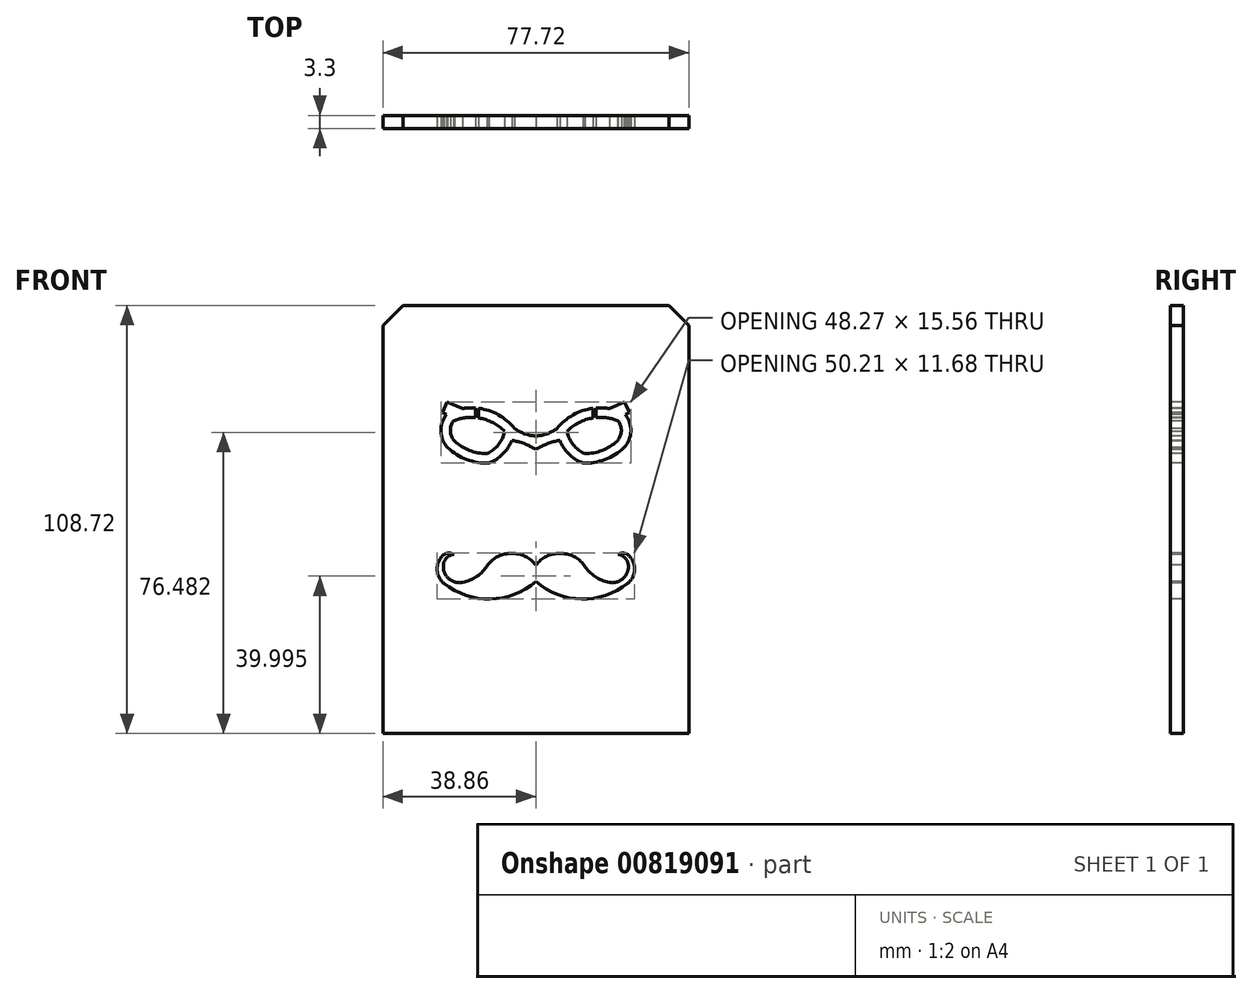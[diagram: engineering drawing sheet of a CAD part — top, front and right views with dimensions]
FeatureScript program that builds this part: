
annotation { "Feature Type Name" : "Feature", "Feature Type Description" : "" }
export const myFeature = defineFeature(function(context is Context, id is Id, definition is map)
    precondition{}
    {
        {
            var Q0;
            Q0=qCreatedBy(makeId("Front.planeOp"),FACE);
            var sketch = newSketch(context, id + "F0", { "sketchPlane" : qUnion([Q0])});
            skLineSegment(sketch, "E0.bottom", {"start": v(38.86, 54.36) * mm, "end": v(-38.86, 54.36) * mm});
            skLineSegment(sketch, "E0.top", {"start": v(38.86, -54.36) * mm, "end": v(-38.86, -54.36) * mm});
            skLineSegment(sketch, "E0.left", {"start": v(38.86, 54.36) * mm, "end": v(38.86, -54.36) * mm});
            skLineSegment(sketch, "E0.right", {"start": v(-38.86, 54.36) * mm, "end": v(-38.86, -54.36) * mm});
            skPoint(sketch, "E0.middle", {"position": v(0, 0) * mm});
            skSolve(sketch);
        }
        {
            var Q0;
            Q0=qSketchRegion(id+"F0",true);
            extrude(context, id + "F1", {"entities" : qUnion([Q0]), "depth" : 3.3 * mm});
        }
        {
            var Q0;
            Q0=makeQuery(id+"F1.opExtrude","CAP_FACE",FACE,{"disambiguationData":[OSD([sQuery(id+"F0.wireOp",EDGE,"E0.bottom"),sQuery(id+"F0.wireOp",EDGE,"E0.top"),sQuery(id+"F0.wireOp",EDGE,"E0.left"),sQuery(id+"F0.wireOp",EDGE,"E0.right")])],"isStart":false});
            var sketch = newSketch(context, id + "F2", { "sketchPlane" : qUnion([Q0])});
            skLineSegment(sketch, "E1", {"start": v(0, 57.24) * mm, "end": v(0, -57.24) * mm, "construction": true});
            skLineSegment(sketch, "E2", {"start": v(-50.8, 0) * mm, "end": v(50.8, 0) * mm, "construction": true});
            skArc(sketch, "E3", {"start": v(35.44, -3.57) * mm, "mid": v(31.46, -11.87) * mm, "end": v(32.26, -21.03) * mm});
            skLineSegment(sketch, "E4", {"start": v(15.88, -44.54) * mm, "end": v(0, -44.54) * mm, "construction": true});
            skArc(sketch, "E5", {"start": v(15.88, -44.54) * mm, "mid": v(30.2, -37.06) * mm, "end": v(32.26, -21.03) * mm});
            skArc(sketch, "E6", {"start": v(15.88, -44.54) * mm, "mid": v(7.78, -45.34) * mm, "end": v(0, -47.71) * mm});
            skArc(sketch, "E7.MirrorCS", {"start": v(-15.87, -44.54) * mm, "mid": v(-7.78, -45.34) * mm, "end": v(0, -47.71) * mm});
            skArc(sketch, "E8.MirrorCS", {"start": v(-15.87, -44.54) * mm, "mid": v(-30.2, -37.06) * mm, "end": v(-32.26, -21.03) * mm});
            skArc(sketch, "E9.MirrorCS", {"start": v(-35.44, -3.57) * mm, "mid": v(-31.46, -11.87) * mm, "end": v(-32.26, -21.03) * mm});
            skArc(sketch, "E10.MirrorCS", {"start": v(-35.44, 3.57) * mm, "mid": v(-31.46, 11.87) * mm, "end": v(-32.26, 21.03) * mm});
            skArc(sketch, "E11.MirrorCS", {"start": v(-15.88, 44.54) * mm, "mid": v(-30.2, 37.06) * mm, "end": v(-32.26, 21.03) * mm});
            skArc(sketch, "E12.MirrorCS", {"start": v(-15.88, 44.54) * mm, "mid": v(-7.78, 45.34) * mm, "end": v(0, 47.71) * mm});
            skArc(sketch, "E13.MirrorCS", {"start": v(15.87, 44.54) * mm, "mid": v(7.78, 45.34) * mm, "end": v(0, 47.71) * mm});
            skArc(sketch, "E14.MirrorCS", {"start": v(15.87, 44.54) * mm, "mid": v(30.2, 37.06) * mm, "end": v(32.26, 21.03) * mm});
            skArc(sketch, "E15.MirrorCS", {"start": v(35.44, 3.57) * mm, "mid": v(31.46, 11.87) * mm, "end": v(32.26, 21.03) * mm});
            skArc(sketch, "E16", {"start": v(35.44, 3.57) * mm, "mid": v(34.41, 0) * mm, "end": v(35.44, -3.57) * mm});
            skPoint(sketch, "E17.orphan", {"position": v(39.69, 0) * mm});
            skArc(sketch, "E18.MirrorCS", {"start": v(-35.44, 3.57) * mm, "mid": v(-34.41, 0) * mm, "end": v(-35.44, -3.57) * mm});
            skPoint(sketch, "E19.orphan", {"position": v(-39.69, 0) * mm});
            skSolve(sketch);
        }
        {
            var Q0;
            Q0=makeQuery(id+"F2.imprint","IMPRINT",FACE,{"disambiguationData":[TD([[makeQuery(id+"F2.imprint","IMPRINT",EDGE,{"derivedFrom":sQuery(id+"F2.wireOp",EDGE,"E3")}),1.0]])]});
            var sketch = newSketch(context, id + "F3", { "sketchPlane" : qUnion([Q0])});
            skFitSpline(sketch, "E20", {"points": [v(-34.74, -25) * mm, v(-17.68, -23.14) * mm, v(0, -25.84) * mm, v(18.3, -28) * mm, v(33.6, -24.4) * mm], "startDerivative": vector(68.08, 28.42) * mm, "endDerivative": vector(41.75, 55.86) * mm});
            skArc(sketch, "E21.0", {"start": v(15.88, -44.54) * mm, "mid": v(28.97, -38.63) * mm, "end": v(33.2, -24.9) * mm});
            skArc(sketch, "E22.0", {"start": v(-15.87, -44.54) * mm, "mid": v(-29.14, -38.43) * mm, "end": v(-33.13, -24.38) * mm});
            skArc(sketch, "E23.0", {"start": v(15.88, -44.54) * mm, "mid": v(7.78, -45.34) * mm, "end": v(0, -47.71) * mm});
            skArc(sketch, "E23.1", {"start": v(-15.87, -44.54) * mm, "mid": v(-7.78, -45.34) * mm, "end": v(0, -47.71) * mm});
            skPoint(sketch, "E24.orphan", {"position": v(-32.26, -21.03) * mm});
            skLineSegment(sketch, "E25.bottom", {"start": v(23.58, -32.65) * mm, "end": v(5.44, -32.65) * mm, "construction": true});
            skLineSegment(sketch, "E25.top", {"start": v(23.58, -12.55) * mm, "end": v(5.44, -12.55) * mm, "construction": true});
            skLineSegment(sketch, "E25.left", {"start": v(23.58, -32.65) * mm, "end": v(23.58, -12.55) * mm, "construction": true});
            skLineSegment(sketch, "E25.right", {"start": v(5.44, -32.65) * mm, "end": v(5.44, -12.55) * mm, "construction": true});
            skArc(sketch, "E26", {"start": v(6.5, -26.77) * mm, "mid": v(6.6, -19.6) * mm, "end": v(5.44, -12.55) * mm});
            skArc(sketch, "E27", {"start": v(23.58, -12.55) * mm, "mid": v(22.47, -20.37) * mm, "end": v(22.78, -28.26) * mm});
            skLineSegment(sketch, "E28", {"start": v(0.57, -13.45) * mm, "end": v(5.44, -12.55) * mm});
            skLineSegment(sketch, "E29", {"start": v(28.46, 0) * mm, "end": v(0.57, 0) * mm, "construction": true});
            skArc(sketch, "E30", {"start": v(-2.4, -8.48) * mm, "mid": v(-2.65, -12) * mm, "end": v(0.57, -13.45) * mm});
            skArc(sketch, "E31", {"start": v(0, -10.42) * mm, "mid": v(-0.23, -8.24) * mm, "end": v(-2.4, -8.48) * mm});
            skArc(sketch, "E32", {"start": v(0, -10.42) * mm, "mid": v(-0.04, -11.92) * mm, "end": v(1.4, -12.35) * mm});
            skArc(sketch, "E33", {"start": v(1.4, -12.35) * mm, "mid": v(5.55, -5.86) * mm, "end": v(0.57, 0) * mm});
            skLineSegment(sketch, "E34", {"start": v(14.51, 0) * mm, "end": v(14.51, -12.55) * mm, "construction": true});
            skArc(sketch, "E35.MirrorCS", {"start": v(27.61, -12.35) * mm, "mid": v(23.47, -5.86) * mm, "end": v(28.46, 0) * mm});
            skLineSegment(sketch, "E36.MirrorCS", {"start": v(28.46, -13.45) * mm, "end": v(23.58, -12.55) * mm});
            skArc(sketch, "E37.MirrorCS", {"start": v(31.42, -8.48) * mm, "mid": v(31.67, -12) * mm, "end": v(28.46, -13.45) * mm});
            skArc(sketch, "E38.MirrorCS", {"start": v(29.02, -10.42) * mm, "mid": v(29.25, -8.24) * mm, "end": v(31.42, -8.48) * mm});
            skArc(sketch, "E39.MirrorCS", {"start": v(29.02, -10.42) * mm, "mid": v(29.06, -11.92) * mm, "end": v(27.61, -12.35) * mm});
            skArc(sketch, "E40", {"start": v(0.57, 0) * mm, "mid": v(5.65, -0.6) * mm, "end": v(10.76, -0.93) * mm});
            skLineSegment(sketch, "E41", {"start": v(10.76, -0.93) * mm, "end": v(8.47, 9.06) * mm});
            skLineSegment(sketch, "E42", {"start": v(8.47, 9.06) * mm, "end": v(6.8, 8.68) * mm});
            skArc(sketch, "E43", {"start": v(7.7, 9.94) * mm, "mid": v(5.6, 10.49) * mm, "end": v(6.8, 8.68) * mm});
            skLineSegment(sketch, "E44", {"start": v(14.51, 0) * mm, "end": v(14.77, 8.31) * mm, "construction": true});
            skLineSegment(sketch, "E45.MirrorCS", {"start": v(18.26, -0.93) * mm, "end": v(21.1, 8.66) * mm});
            skLineSegment(sketch, "E46.MirrorCS", {"start": v(21.1, 8.66) * mm, "end": v(22.75, 8.18) * mm});
            skArc(sketch, "E47.MirrorCS", {"start": v(21.93, 9.5) * mm, "mid": v(24.07, 9.9) * mm, "end": v(22.75, 8.18) * mm});
            skArc(sketch, "E48", {"start": v(7.7, 9.94) * mm, "mid": v(12.62, 15.22) * mm, "end": v(14.1, 22.28) * mm});
            skArc(sketch, "E49", {"start": v(15.59, 22.28) * mm, "mid": v(17.1, 15.06) * mm, "end": v(21.93, 9.5) * mm});
            skLineSegment(sketch, "E50", {"start": v(14.1, 22.28) * mm, "end": v(12.75, 29.94) * mm});
            skLineSegment(sketch, "E51", {"start": v(12.75, 29.94) * mm, "end": v(10.25, 29.5) * mm});
            skLineSegment(sketch, "E52", {"start": v(10.25, 29.5) * mm, "end": v(10.04, 30.72) * mm});
            skLineSegment(sketch, "E53", {"start": v(10.04, 30.72) * mm, "end": v(12.66, 31.3) * mm});
            skLineSegment(sketch, "E54", {"start": v(12.66, 31.3) * mm, "end": v(12.12, 34.79) * mm});
            skLineSegment(sketch, "E55", {"start": v(12.12, 34.79) * mm, "end": v(14.24, 35.11) * mm});
            skLineSegment(sketch, "E56", {"start": v(14.24, 35.11) * mm, "end": v(14.8, 31.45) * mm});
            skLineSegment(sketch, "E57", {"start": v(14.8, 31.45) * mm, "end": v(17.72, 31.9) * mm});
            skLineSegment(sketch, "E58", {"start": v(17.72, 31.9) * mm, "end": v(17.99, 30.17) * mm});
            skLineSegment(sketch, "E59", {"start": v(17.99, 30.17) * mm, "end": v(14.89, 29.68) * mm});
            skLineSegment(sketch, "E60", {"start": v(14.89, 29.68) * mm, "end": v(15.59, 22.28) * mm});
            skArc(sketch, "E61.trimOffspring", {"start": v(18.26, -0.93) * mm, "mid": v(23.37, -0.6) * mm, "end": v(28.46, 0) * mm});
            skPoint(sketch, "E62.orphan", {"position": v(18.2, -1.17) * mm});
            skLineSegment(sketch, "E63", {"start": v(8.48, -4.98) * mm, "end": v(9.12, -7.41) * mm});
            skLineSegment(sketch, "E64", {"start": v(9.77, -9.85) * mm, "end": v(10.94, -9.54) * mm});
            skLineSegment(sketch, "E65", {"start": v(12.72, -9.06) * mm, "end": v(12.26, -7.34) * mm});
            skLineSegment(sketch, "E66", {"start": v(11.56, -4.7) * mm, "end": v(10.33, -4.82) * mm});
            skLineSegment(sketch, "E67", {"start": v(9.75, -4.87) * mm, "end": v(10.34, -7.13) * mm});
            skLineSegment(sketch, "E68", {"start": v(10.34, -7.13) * mm, "end": v(9.12, -7.41) * mm});
            skLineSegment(sketch, "E69", {"start": v(10.33, -4.82) * mm, "end": v(10.9, -7.06) * mm});
            skLineSegment(sketch, "E70", {"start": v(10.9, -7.06) * mm, "end": v(12.14, -6.89) * mm});
            skLineSegment(sketch, "E71", {"start": v(9.29, -8.05) * mm, "end": v(10.46, -7.73) * mm});
            skLineSegment(sketch, "E72", {"start": v(10.46, -7.73) * mm, "end": v(10.94, -9.54) * mm});
            skLineSegment(sketch, "E73", {"start": v(11.57, -9.37) * mm, "end": v(11.12, -7.64) * mm});
            skLineSegment(sketch, "E74", {"start": v(11.12, -7.64) * mm, "end": v(12.26, -7.34) * mm});
            skLineSegment(sketch, "E75.trimOffspring", {"start": v(12.14, -6.89) * mm, "end": v(11.56, -4.7) * mm});
            skLineSegment(sketch, "E76.trimOffspring", {"start": v(9.75, -4.87) * mm, "end": v(8.48, -4.98) * mm});
            skLineSegment(sketch, "E77.trimOffspring", {"start": v(9.29, -8.05) * mm, "end": v(9.77, -9.85) * mm});
            skLineSegment(sketch, "E78.trimOffspring", {"start": v(11.57, -9.37) * mm, "end": v(12.72, -9.06) * mm});
            skLineSegment(sketch, "E79.MirrorCS", {"start": v(17.46, -4.7) * mm, "end": v(18.69, -4.82) * mm});
            skLineSegment(sketch, "E80.MirrorCS", {"start": v(19.27, -4.87) * mm, "end": v(18.68, -7.13) * mm});
            skLineSegment(sketch, "E81.MirrorCS", {"start": v(17.45, -9.37) * mm, "end": v(17.9, -7.64) * mm});
            skLineSegment(sketch, "E82.MirrorCS", {"start": v(18.68, -7.13) * mm, "end": v(19.9, -7.41) * mm});
            skLineSegment(sketch, "E83.MirrorCS", {"start": v(17.9, -7.64) * mm, "end": v(16.76, -7.34) * mm});
            skLineSegment(sketch, "E84.MirrorCS", {"start": v(18.69, -4.82) * mm, "end": v(18.12, -7.06) * mm});
            skLineSegment(sketch, "E85.MirrorCS", {"start": v(16.88, -6.89) * mm, "end": v(17.46, -4.7) * mm});
            skLineSegment(sketch, "E86.MirrorCS", {"start": v(18.12, -7.06) * mm, "end": v(16.88, -6.89) * mm});
            skLineSegment(sketch, "E87.MirrorCS", {"start": v(19.27, -4.87) * mm, "end": v(20.54, -4.98) * mm});
            skLineSegment(sketch, "E88.MirrorCS", {"start": v(20.54, -4.98) * mm, "end": v(19.9, -7.41) * mm});
            skLineSegment(sketch, "E89.MirrorCS", {"start": v(19.73, -8.05) * mm, "end": v(18.56, -7.73) * mm});
            skLineSegment(sketch, "E90.MirrorCS", {"start": v(19.73, -8.05) * mm, "end": v(19.25, -9.85) * mm});
            skLineSegment(sketch, "E91.MirrorCS", {"start": v(19.25, -9.85) * mm, "end": v(18.08, -9.54) * mm});
            skLineSegment(sketch, "E92.MirrorCS", {"start": v(18.56, -7.73) * mm, "end": v(18.08, -9.54) * mm});
            skLineSegment(sketch, "E93.MirrorCS", {"start": v(17.45, -9.37) * mm, "end": v(16.3, -9.06) * mm});
            skLineSegment(sketch, "E94.MirrorCS", {"start": v(16.3, -9.06) * mm, "end": v(16.76, -7.34) * mm});
            skArc(sketch, "E95", {"start": v(14.28, 11.97) * mm, "mid": v(12.23, 10.98) * mm, "end": v(11.15, 8.98) * mm});
            skLineSegment(sketch, "E96", {"start": v(14.28, 11.97) * mm, "end": v(14.28, 8.98) * mm});
            skLineSegment(sketch, "E97", {"start": v(15.17, 4.65) * mm, "end": v(15.17, 7.88) * mm});
            skLineSegment(sketch, "E98", {"start": v(18.4, 8.98) * mm, "end": v(15.17, 8.98) * mm});
            skLineSegment(sketch, "E99", {"start": v(11.1, 7.88) * mm, "end": v(14.28, 7.88) * mm});
            skLineSegment(sketch, "E100.trimOffspring", {"start": v(15.17, 8.98) * mm, "end": v(15.17, 11.98) * mm});
            skLineSegment(sketch, "E101.trimOffspring", {"start": v(15.17, 7.88) * mm, "end": v(18.43, 7.88) * mm});
            skLineSegment(sketch, "E102.trimOffspring", {"start": v(14.28, 7.88) * mm, "end": v(14.28, 4.66) * mm});
            skLineSegment(sketch, "E103.trimOffspring", {"start": v(14.28, 8.98) * mm, "end": v(11.15, 8.98) * mm});
            skArc(sketch, "E104.trimOffspring", {"start": v(11.1, 7.88) * mm, "mid": v(12.14, 5.73) * mm, "end": v(14.28, 4.66) * mm});
            skArc(sketch, "E105.trimOffspring", {"start": v(18.4, 8.98) * mm, "mid": v(17.28, 11.01) * mm, "end": v(15.17, 11.98) * mm});
            skArc(sketch, "E106.trimOffspring", {"start": v(15.17, 4.65) * mm, "mid": v(17.37, 5.7) * mm, "end": v(18.43, 7.88) * mm});
            skLineSegment(sketch, "E107.left", {"start": v(12.04, -27.4) * mm, "end": v(12.04, -21.48) * mm});
            skLineSegment(sketch, "E107.right", {"start": v(16, -27.8) * mm, "end": v(16, -21.48) * mm});
            skArc(sketch, "E108", {"start": v(16, -21.48) * mm, "mid": v(14.02, -19.5) * mm, "end": v(12.04, -21.48) * mm});
            skLineSegment(sketch, "E109", {"start": v(12.04, -27.4) * mm, "end": v(16, -27.8) * mm});
            skArc(sketch, "E110.0", {"start": v(-35.44, -3.57) * mm, "mid": v(-31.46, -11.87) * mm, "end": v(-32.26, -21.03) * mm, "construction": true});
            skArc(sketch, "E110.1", {"start": v(15.87, 44.54) * mm, "mid": v(7.78, 45.34) * mm, "end": v(0, 47.71) * mm});
            skArc(sketch, "E110.2", {"start": v(-15.88, 44.54) * mm, "mid": v(-30.2, 37.06) * mm, "end": v(-32.26, 21.03) * mm, "construction": true});
            skArc(sketch, "E110.3", {"start": v(-35.44, 3.57) * mm, "mid": v(-34.41, 0) * mm, "end": v(-35.44, -3.57) * mm, "construction": true});
            skArc(sketch, "E110.4", {"start": v(-35.44, 3.57) * mm, "mid": v(-31.46, 11.87) * mm, "end": v(-32.26, 21.03) * mm});
            skArc(sketch, "E110.5", {"start": v(-15.88, 44.54) * mm, "mid": v(-7.78, 45.34) * mm, "end": v(0, 47.71) * mm});
            skArc(sketch, "E111", {"start": v(-17.1, 9.66) * mm, "mid": v(-3.37, 14.89) * mm, "end": v(1.5, 28.74) * mm});
            skArc(sketch, "E112", {"start": v(-17.1, 9.66) * mm, "mid": v(-26.87, 8.42) * mm, "end": v(-35.44, 3.57) * mm});
            skArc(sketch, "E113", {"start": v(15.87, 44.54) * mm, "mid": v(5.2, 39.82) * mm, "end": v(1.5, 28.74) * mm});
            skArc(sketch, "E114.trimOffspring", {"start": v(-15.88, 44.54) * mm, "mid": v(-30.2, 37.06) * mm, "end": v(-32.26, 21.03) * mm});
            skArc(sketch, "E115", {"start": v(-24.92, -22.89) * mm, "mid": v(-23.55, -16.2) * mm, "end": v(-24.4, -9.44) * mm});
            skFitSpline(sketch, "E116", {"points": [v(-24.4, -9.44) * mm, v(-26.98, -10.38) * mm, v(-27.97, -8.39) * mm, v(-29.93, -8.52) * mm, v(-30.92, -6) * mm, v(-32.1, -5.52) * mm, v(-32.53, -4.18) * mm, v(-32.18, -3.27) * mm, v(-31.84, -4.44) * mm, v(-31.05, -4.83) * mm, v(-31.49, -2) * mm, v(-30.88, -2.14) * mm, v(-30.1, -5.05) * mm, v(-29.45, -3.57) * mm, v(-28.71, -3.66) * mm, v(-29.54, -5.78) * mm, v(-29.23, -7.17) * mm, v(-27.54, -7.04) * mm, v(-26.28, -8.52) * mm, v(-24.4, -7.6) * mm], "startDerivative": vector(-46.53, -30.94) * mm, "endDerivative": vector(36.03, 29.74) * mm});
            skArc(sketch, "E117", {"start": v(-24.4, -7.6) * mm, "mid": v(-24.93, -4.98) * mm, "end": v(-25.9, -2.49) * mm});
            skFitSpline(sketch, "E118", {"points": [v(-25.9, -2.49) * mm, v(-27.5, -1.49) * mm, v(-28.76, -1.49) * mm, v(-29.23, 0) * mm, v(-31.14, 0) * mm, v(-30.8, 3.42) * mm, v(-29.97, 3.55) * mm, v(-30.27, 1.77) * mm, v(-29.54, 1.72) * mm, v(-28.8, 4.59) * mm, v(-27.67, 4.37) * mm, v(-28.28, 1.98) * mm, v(-27.84, 0) * mm, v(-27.2, 2.46) * mm, v(-25.9, 2.37) * mm, v(-25.9, 0) * mm, v(-24.11, -2.49) * mm, v(-22.72, -5.26) * mm, v(-21.68, -4.18) * mm, v(-23.16, 1.33) * mm, v(-20.82, 1.46) * mm, v(-20.82, 3.02) * mm], "startDerivative": vector(-33.14, 31.82) * mm, "endDerivative": vector(-15.18, 49.9) * mm});
            skFitSpline(sketch, "E119", {"points": [v(-20.82, 3.02) * mm, v(-19.2, 3.92) * mm, v(-20.04, 5.84) * mm, v(-20.82, 8.3) * mm, v(-20.04, 8.38) * mm, v(-19.62, 6.46) * mm, v(-18.62, 5.34) * mm, v(-18.96, 7.3) * mm, v(-18.2, 7.55) * mm, v(-18.12, 4.13) * mm, v(-19.33, 2.25) * mm, v(-19.46, 0.87) * mm, v(-20.82, 0) * mm, v(-20.04, -3.35) * mm, v(-16.32, 0) * mm, v(-17.1, 1.46) * mm, v(-15.74, 3.02) * mm, v(-15.45, 5.84) * mm, v(-14.49, 5.55) * mm, v(-14.82, 3.02) * mm, v(-14.53, 1.46) * mm, v(-13.36, 4) * mm, v(-12.02, 3.02) * mm, v(-14.2, 0) * mm, v(-17.1, -4.06) * mm, v(-17.1, -7.4) * mm, v(-14.36, -5.44) * mm, v(-14.57, -4.1) * mm, v(-12.78, -3.22) * mm, v(-12.53, -1.68) * mm, v(-10.44, -0.8) * mm, v(-10.27, 1.46) * mm, v(-9.35, 0) * mm, v(-8.6, 3.02) * mm, v(-8.1, 0) * mm, v(-9.44, -1.26) * mm, v(-11.31, -3.26) * mm, v(-13.15, -4.6) * mm, v(-13.36, -6.6) * mm, v(-15.78, -8.94) * mm], "startDerivative": vector(94.65, 30.69) * mm, "endDerivative": vector(-102.82, -69.25) * mm});
            skArc(sketch, "E120", {"start": v(-15.78, -8.94) * mm, "mid": v(-16.8, -16.14) * mm, "end": v(-15.78, -23.34) * mm});
            skFitSpline(sketch, "E121", {"points": [v(-22.4, -11.55) * mm, v(-21.43, -13.07) * mm, v(-21.4, -14.11) * mm, v(-20.72, -14.36) * mm, v(-20.54, -13.59) * mm, v(-20.94, -12.02) * mm, v(-21.71, -11.06) * mm, v(-22.67, -10.07) * mm, v(-22.4, -11.55) * mm]});
            skFitSpline(sketch, "E122", {"points": [v(-18.38, -10.1) * mm, v(-19.09, -11.5) * mm, v(-19.21, -12.7) * mm, v(-19.15, -14.02) * mm, v(-18.84, -14.6) * mm, v(-18.38, -14.05) * mm, v(-18.26, -13.1) * mm, v(-18.56, -12.32) * mm, v(-18.29, -11.28) * mm, v(-17.6, -10.38) * mm, v(-18.38, -10.1) * mm]});
            skFitSpline(sketch, "E123", {"points": [v(-20.3, -15.78) * mm, v(-20.35, -17.1) * mm, v(-20.9, -18.47) * mm, v(-21.8, -19.67) * mm, v(-21.9, -21.46) * mm, v(-20.45, -21.43) * mm, v(-19.64, -20.38) * mm, v(-19.43, -18.84) * mm, v(-19.7, -17.85) * mm, v(-19.7, -16.37) * mm, v(-19.43, -15.38) * mm, v(-20.3, -15.78) * mm]});
            skCircle(sketch, "E124", {"center": v(-15.88, 27.08) * mm, "radius": 13.34 * mm});
            skSolve(sketch);
        }
        {
            var Q0;
            Q0=qSketchRegion(id+"F3",true);
            extrude(context, id + "F4", {"entities" : qUnion([Q0]), "operationType" : NewBodyOperationType.ADD, "oppositeDirection" : true, "depth" : 3.3 * mm});
        }
        {
            var Q0;
            Q0=makeQuery(id+"F1.opExtrude","SWEPT_EDGE",EDGE,{"disambiguationData":[OSD([sQuery(id+"F0.wireOp",EDGE,"E0.bottom"),sQuery(id+"F0.wireOp",EDGE,"E0.right")])]});
            var Q1;
            Q1=makeQuery(id+"F1.opExtrude","SWEPT_EDGE",EDGE,{"disambiguationData":[OSD([sQuery(id+"F0.wireOp",EDGE,"E0.bottom"),sQuery(id+"F0.wireOp",EDGE,"E0.left")])]});
            chamfer(context, id + "F5", {"entities" : qUnion([Q0, Q1]), "width" : 5.08 * mm, "tangentPropagation" : true});
        }
        {
            var Q0;
            Q0=makeQuery(id+"F2.imprint","IMPRINT",FACE,{"disambiguationData":[TD([[makeQuery(id+"F2.imprint","IMPRINT",EDGE,{"derivedFrom":sQuery(id+"F2.wireOp",EDGE,"E3")}),-1.0]])]});
            var sketch = newSketch(context, id + "F6", { "sketchPlane" : qUnion([Q0])});
            skArc(sketch, "E125", {"start": v(6.08, 20.1) * mm, "mid": v(8.4, 16.62) * mm, "end": v(11.92, 14.34) * mm});
            skArc(sketch, "E126", {"start": v(11.92, 14.34) * mm, "mid": v(17.55, 15.25) * mm, "end": v(22.4, 18.27) * mm});
            skArc(sketch, "E127", {"start": v(22.4, 18.27) * mm, "mid": v(24.13, 22.42) * mm, "end": v(22.71, 26.69) * mm});
            skArc(sketch, "E128", {"start": v(18.65, 28.2) * mm, "mid": v(16.98, 28.36) * mm, "end": v(15.3, 28.33) * mm});
            skArc(sketch, "E129.0", {"start": v(20.92, 25.07) * mm, "mid": v(18.16, 25.83) * mm, "end": v(15.3, 25.9) * mm});
            skArc(sketch, "E129.1", {"start": v(20.68, 19.97) * mm, "mid": v(21.72, 22.48) * mm, "end": v(20.92, 25.07) * mm});
            skArc(sketch, "E129.2", {"start": v(12.43, 16.74) * mm, "mid": v(16.86, 17.57) * mm, "end": v(20.68, 19.97) * mm});
            skArc(sketch, "E129.3", {"start": v(7.92, 22.36) * mm, "mid": v(9.5, 19) * mm, "end": v(12.43, 16.74) * mm});
            skArc(sketch, "E130", {"start": v(0, 21.24) * mm, "mid": v(2.83, 21.78) * mm, "end": v(5.38, 23.13) * mm});
            skArc(sketch, "E131", {"start": v(6.08, 20.1) * mm, "mid": v(2.93, 19.26) * mm, "end": v(0, 17.8) * mm});
            skLineSegment(sketch, "E132", {"start": v(18.65, 28.2) * mm, "end": v(22.54, 29.9) * mm});
            skLineSegment(sketch, "E133", {"start": v(22.54, 29.9) * mm, "end": v(23.75, 27.14) * mm});
            skLineSegment(sketch, "E134", {"start": v(23.75, 27.14) * mm, "end": v(22.71, 26.69) * mm});
            skPoint(sketch, "E135.orphan", {"position": v(22.4, 27.06) * mm});
            skArc(sketch, "E136", {"start": v(0, -15.75) * mm, "mid": v(11.58, -20.2) * mm, "end": v(23.33, -16.24) * mm});
            skArc(sketch, "E137", {"start": v(23.33, -16.24) * mm, "mid": v(25.1, -12.56) * mm, "end": v(23.33, -8.89) * mm});
            skArc(sketch, "E138", {"start": v(23.33, -8.89) * mm, "mid": v(22.07, -8.52) * mm, "end": v(20.8, -8.89) * mm});
            skArc(sketch, "E139", {"start": v(23.33, -10.83) * mm, "mid": v(22.38, -9.45) * mm, "end": v(20.8, -8.89) * mm});
            skArc(sketch, "E140", {"start": v(18.65, -15.99) * mm, "mid": v(22.45, -14.73) * mm, "end": v(23.33, -10.83) * mm});
            skArc(sketch, "E141", {"start": v(12.27, -11.6) * mm, "mid": v(15, -14.45) * mm, "end": v(18.65, -15.99) * mm});
            skArc(sketch, "E142", {"start": v(12.27, -11.6) * mm, "mid": v(6.14, -8.58) * mm, "end": v(0, -11.6) * mm});
            skArc(sketch, "E143.MirrorCS", {"start": v(-12.27, -11.6) * mm, "mid": v(-6.14, -8.58) * mm, "end": v(0, -11.6) * mm});
            skArc(sketch, "E144.MirrorCS", {"start": v(-12.27, -11.6) * mm, "mid": v(-15, -14.45) * mm, "end": v(-18.65, -15.99) * mm});
            skArc(sketch, "E145.MirrorCS", {"start": v(0, -15.75) * mm, "mid": v(-11.58, -20.2) * mm, "end": v(-23.33, -16.24) * mm});
            skArc(sketch, "E146.MirrorCS", {"start": v(-23.33, -16.24) * mm, "mid": v(-25.1, -12.56) * mm, "end": v(-23.33, -8.89) * mm});
            skArc(sketch, "E147.MirrorCS", {"start": v(-23.33, -8.89) * mm, "mid": v(-22.07, -8.52) * mm, "end": v(-20.8, -8.89) * mm});
            skArc(sketch, "E148.MirrorCS", {"start": v(-23.33, -10.83) * mm, "mid": v(-22.38, -9.45) * mm, "end": v(-20.8, -8.89) * mm});
            skArc(sketch, "E149.MirrorCS", {"start": v(-18.65, -15.99) * mm, "mid": v(-22.45, -14.73) * mm, "end": v(-23.33, -10.83) * mm});
            skArc(sketch, "E150.MirrorCS", {"start": v(0, 21.24) * mm, "mid": v(-2.83, 21.78) * mm, "end": v(-5.38, 23.13) * mm});
            skArc(sketch, "E151.MirrorCS", {"start": v(-6.08, 20.1) * mm, "mid": v(-2.93, 19.26) * mm, "end": v(0, 17.8) * mm});
            skArc(sketch, "E152.MirrorCS", {"start": v(-6.08, 20.1) * mm, "mid": v(-8.4, 16.62) * mm, "end": v(-11.92, 14.34) * mm});
            skArc(sketch, "E153.MirrorCS", {"start": v(-11.92, 14.34) * mm, "mid": v(-17.55, 15.25) * mm, "end": v(-22.4, 18.27) * mm});
            skArc(sketch, "E154.MirrorCS", {"start": v(-12.43, 16.74) * mm, "mid": v(-16.86, 17.57) * mm, "end": v(-20.68, 19.97) * mm});
            skArc(sketch, "E155.MirrorCS", {"start": v(-22.4, 18.27) * mm, "mid": v(-24.13, 22.42) * mm, "end": v(-22.71, 26.69) * mm});
            skLineSegment(sketch, "E156.MirrorCS", {"start": v(-23.75, 27.14) * mm, "end": v(-22.71, 26.69) * mm});
            skLineSegment(sketch, "E157.MirrorCS", {"start": v(-22.54, 29.9) * mm, "end": v(-23.75, 27.14) * mm});
            skLineSegment(sketch, "E158.MirrorCS", {"start": v(-18.65, 28.2) * mm, "end": v(-22.54, 29.9) * mm});
            skArc(sketch, "E159.MirrorCS", {"start": v(-18.65, 28.2) * mm, "mid": v(-16.98, 28.36) * mm, "end": v(-15.3, 28.33) * mm});
            skArc(sketch, "E160.MirrorCS", {"start": v(-7.92, 22.36) * mm, "mid": v(-9.5, 19) * mm, "end": v(-12.43, 16.74) * mm});
            skArc(sketch, "E161.MirrorCS", {"start": v(-20.68, 19.97) * mm, "mid": v(-21.72, 22.48) * mm, "end": v(-20.92, 25.07) * mm});
            skArc(sketch, "E162.MirrorCS", {"start": v(-20.92, 25.07) * mm, "mid": v(-18.16, 25.83) * mm, "end": v(-15.3, 25.9) * mm});
            skLineSegment(sketch, "E163.left", {"start": v(-15.3, 28.33) * mm, "end": v(-15.3, 25.9) * mm});
            skLineSegment(sketch, "E163.right", {"start": v(-14.51, 28.24) * mm, "end": v(-14.51, 25.8) * mm});
            skArc(sketch, "E164.trimOffspring", {"start": v(-14.51, 28.24) * mm, "mid": v(-9.46, 26.56) * mm, "end": v(-5.38, 23.13) * mm});
            skArc(sketch, "E165.trimOffspring", {"start": v(-14.51, 25.8) * mm, "mid": v(-10.94, 24.61) * mm, "end": v(-7.92, 22.36) * mm});
            skLineSegment(sketch, "E166.MirrorCS", {"start": v(14.51, 28.24) * mm, "end": v(14.51, 25.8) * mm});
            skLineSegment(sketch, "E167.MirrorCS", {"start": v(15.3, 28.33) * mm, "end": v(15.3, 25.9) * mm});
            skArc(sketch, "E168.trimOffspring", {"start": v(14.51, 28.24) * mm, "mid": v(9.46, 26.56) * mm, "end": v(5.38, 23.13) * mm});
            skArc(sketch, "E169.trimOffspring", {"start": v(14.51, 25.8) * mm, "mid": v(10.94, 24.61) * mm, "end": v(7.92, 22.36) * mm});
            skSolve(sketch);
        }
        {
            var Q0;
            Q0=qSketchRegion(id+"F6",true);
            extrude(context, id + "F7", {"entities" : qUnion([Q0]), "operationType" : NewBodyOperationType.REMOVE, "endBound" : BoundingType.THROUGH_ALL, "oppositeDirection" : true, "depth" : 25.4 * mm});
        }
    });
